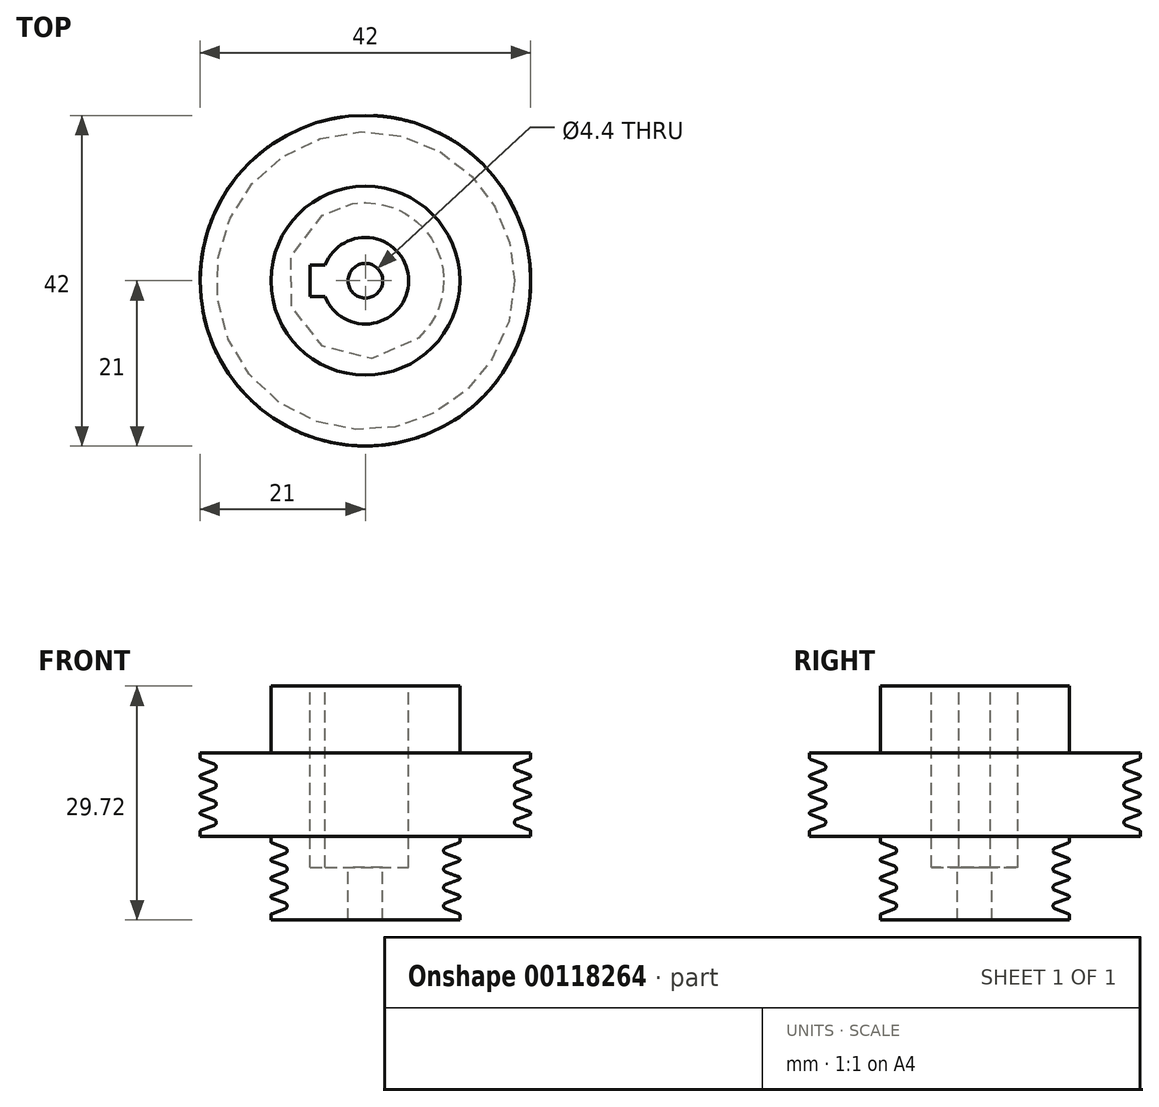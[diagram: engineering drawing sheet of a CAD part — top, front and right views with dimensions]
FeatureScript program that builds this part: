
annotation { "Feature Type Name" : "Feature", "Feature Type Description" : "" }
export const myFeature = defineFeature(function(context is Context, id is Id, definition is map)
    precondition{}
    {
        {
            var Q0;
            Q0=qCreatedBy(makeId("Front.planeOp"),FACE);
            var sketch = newSketch(context, id + "F0", { "sketchPlane" : qUnion([Q0])});
            skLineSegment(sketch, "E0", {"start": v(0, 0) * mm, "end": v(-5.5, 0) * mm, "construction": true});
            skLineSegment(sketch, "E1", {"start": v(-5.5, 0) * mm, "end": v(-21, 0) * mm});
            skLineSegment(sketch, "E2", {"start": v(-21, 1.8) * mm, "end": v(-21, 0.63) * mm, "construction": true});
            skLineSegment(sketch, "E3", {"start": v(-21, 1.8) * mm, "end": v(-19.34, 1.8) * mm, "construction": true});
            skArc(sketch, "E4", {"start": v(-19.2, 1.42) * mm, "mid": v(-18.94, 1.8) * mm, "end": v(-19.2, 2.18) * mm});
            skLineSegment(sketch, "E5", {"start": v(-21, 0.63) * mm, "end": v(-20.8, 0.63) * mm, "construction": true});
            skArc(sketch, "E6", {"start": v(-20.87, 0.82) * mm, "mid": v(-20.96, 0.74) * mm, "end": v(-21, 0.63) * mm});
            skLineSegment(sketch, "E7", {"start": v(-20.87, 0.82) * mm, "end": v(-19.2, 1.42) * mm});
            skLineSegment(sketch, "E8", {"start": v(-19.34, 1.8) * mm, "end": v(-18.94, 1.8) * mm, "construction": true});
            skLineSegment(sketch, "E9.MirrorCS", {"start": v(-20.87, 2.78) * mm, "end": v(-19.2, 2.18) * mm});
            skArc(sketch, "E10.MirrorC", {"start": v(-20.87, 2.78) * mm, "mid": v(-21, 2.97) * mm, "end": v(-20.87, 3.16) * mm});
            skLineSegment(sketch, "E11", {"start": v(-21, 1.8) * mm, "end": v(-21, 10.62) * mm, "construction": true});
            skLineSegment(sketch, "E12", {"start": v(-21, 0.63) * mm, "end": v(-21, 0) * mm});
            skLineSegment(sketch, "E13", {"start": v(-21, 2.97) * mm, "end": v(-20.8, 2.97) * mm, "construction": true});
            skLineSegment(sketch, "E14.MirrorCS", {"start": v(-20.87, 5.12) * mm, "end": v(-19.2, 4.52) * mm});
            skLineSegment(sketch, "E15.MirrorCS", {"start": v(-20.87, 3.16) * mm, "end": v(-19.2, 3.76) * mm});
            skArc(sketch, "E16.MirrorCS", {"start": v(-19.2, 4.52) * mm, "mid": v(-18.94, 4.14) * mm, "end": v(-19.2, 3.76) * mm});
            skArc(sketch, "E17.MirrorC", {"start": v(-20.87, 3.16) * mm, "mid": v(-21, 2.97) * mm, "end": v(-20.87, 2.78) * mm});
            skLineSegment(sketch, "E18", {"start": v(-21.58, 4.14) * mm, "end": v(-21, 4.14) * mm});
            skArc(sketch, "E19.MirrorC", {"start": v(-20.87, 5.12) * mm, "mid": v(-21, 5.3) * mm, "end": v(-20.87, 5.5) * mm});
            skLineSegment(sketch, "E20", {"start": v(-21, 5.3) * mm, "end": v(-20.8, 5.3) * mm, "construction": true});
            skLineSegment(sketch, "E21.MirrorCS", {"start": v(-20.87, 5.5) * mm, "end": v(-19.2, 6.1) * mm});
            skArc(sketch, "E22.MirrorCS", {"start": v(-19.2, 6.1) * mm, "mid": v(-18.94, 6.48) * mm, "end": v(-19.2, 6.86) * mm});
            skLineSegment(sketch, "E23.MirrorCS", {"start": v(-20.87, 7.46) * mm, "end": v(-19.2, 6.86) * mm});
            skArc(sketch, "E24.MirrorCS", {"start": v(-20.87, 7.84) * mm, "mid": v(-21, 7.65) * mm, "end": v(-20.87, 7.46) * mm});
            skLineSegment(sketch, "E25.MirrorCS", {"start": v(-20.87, 7.84) * mm, "end": v(-19.2, 8.44) * mm});
            skArc(sketch, "E26.MirrorCS", {"start": v(-19.2, 9.2) * mm, "mid": v(-18.94, 8.82) * mm, "end": v(-19.2, 8.44) * mm});
            skLineSegment(sketch, "E27.MirrorCS", {"start": v(-20.87, 9.8) * mm, "end": v(-19.2, 9.2) * mm});
            skArc(sketch, "E28.MirrorCS", {"start": v(-20.87, 9.8) * mm, "mid": v(-20.96, 9.87) * mm, "end": v(-21, 9.99) * mm});
            skLineSegment(sketch, "E29.MirrorCS", {"start": v(-21, 9.99) * mm, "end": v(-21, 10.62) * mm});
            skLineSegment(sketch, "E30.MirrorCS", {"start": v(-5.5, 10.62) * mm, "end": v(-21, 10.62) * mm});
            skLineSegment(sketch, "E31.MirrorCS", {"start": v(0, 10.62) * mm, "end": v(-5.5, 10.62) * mm, "construction": true});
            skLineSegment(sketch, "E32", {"start": v(-5.5, 10.62) * mm, "end": v(-5.5, 0) * mm});
            skLineSegment(sketch, "E33", {"start": v(0, 10.62) * mm, "end": v(0, 0) * mm, "construction": true});
            skArc(sketch, "E34", {"start": v(-10.2, -2.18) * mm, "mid": v(-9.94, -1.8) * mm, "end": v(-10.2, -1.42) * mm});
            skArc(sketch, "E35", {"start": v(-12, -0.63) * mm, "mid": v(-11.96, -0.74) * mm, "end": v(-11.87, -0.82) * mm});
            skLineSegment(sketch, "E36", {"start": v(-11.87, -0.82) * mm, "end": v(-10.2, -1.42) * mm});
            skLineSegment(sketch, "E37", {"start": v(-12, -0.63) * mm, "end": v(-12, 0) * mm});
            skLineSegment(sketch, "E38", {"start": v(-12.57, -1.8) * mm, "end": v(-7.09, -1.8) * mm, "construction": true});
            skLineSegment(sketch, "E39.MirrorCS", {"start": v(-11.87, -2.78) * mm, "end": v(-10.2, -2.18) * mm});
            skArc(sketch, "E40.MirrorC", {"start": v(-11.87, -3.16) * mm, "mid": v(-12, -2.97) * mm, "end": v(-11.87, -2.78) * mm});
            skLineSegment(sketch, "E41", {"start": v(-12.6, -2.97) * mm, "end": v(-7.04, -2.97) * mm, "construction": true});
            skArc(sketch, "E42.MirrorC", {"start": v(-11.87, -5.5) * mm, "mid": v(-12, -5.31) * mm, "end": v(-11.87, -5.12) * mm});
            skArc(sketch, "E43.MirrorC", {"start": v(-10.2, -3.76) * mm, "mid": v(-9.94, -4.14) * mm, "end": v(-10.2, -4.52) * mm});
            skLineSegment(sketch, "E44.MirrorCS", {"start": v(-11.87, -3.16) * mm, "end": v(-10.2, -3.76) * mm});
            skLineSegment(sketch, "E45.MirrorCS", {"start": v(-11.87, -5.12) * mm, "end": v(-10.2, -4.52) * mm});
            skLineSegment(sketch, "E46", {"start": v(-12.93, -5.31) * mm, "end": v(-7.12, -5.31) * mm, "construction": true});
            skLineSegment(sketch, "E47.MirrorCS", {"start": v(-11.87, -5.5) * mm, "end": v(-10.2, -6.1) * mm});
            skArc(sketch, "E48.MirrorC", {"start": v(-10.2, -6.86) * mm, "mid": v(-9.94, -6.48) * mm, "end": v(-10.2, -6.1) * mm});
            skLineSegment(sketch, "E49.MirrorCS", {"start": v(-11.87, -7.46) * mm, "end": v(-10.2, -6.86) * mm});
            skArc(sketch, "E50.MirrorC", {"start": v(-11.87, -7.46) * mm, "mid": v(-12, -7.65) * mm, "end": v(-11.87, -7.84) * mm});
            skLineSegment(sketch, "E51.MirrorCS", {"start": v(-11.87, -7.84) * mm, "end": v(-10.2, -8.44) * mm});
            skArc(sketch, "E52.MirrorC", {"start": v(-10.2, -8.44) * mm, "mid": v(-9.94, -8.82) * mm, "end": v(-10.2, -9.2) * mm});
            skLineSegment(sketch, "E53.MirrorCS", {"start": v(-11.87, -9.8) * mm, "end": v(-10.2, -9.2) * mm});
            skArc(sketch, "E54.MirrorC", {"start": v(-12, -10) * mm, "mid": v(-11.96, -9.88) * mm, "end": v(-11.87, -9.8) * mm});
            skLineSegment(sketch, "E55.MirrorCS", {"start": v(-12, -10) * mm, "end": v(-12, -10.62) * mm});
            skLineSegment(sketch, "E56", {"start": v(0, -10.62) * mm, "end": v(0, 0) * mm, "construction": true});
            skLineSegment(sketch, "E57", {"start": v(-5.5, 0) * mm, "end": v(-5.5, -10.62) * mm});
            skLineSegment(sketch, "E58", {"start": v(-12, -10.62) * mm, "end": v(-5.5, -10.62) * mm});
            skLineSegment(sketch, "E59", {"start": v(-5.5, -10.62) * mm, "end": v(0, -10.62) * mm, "construction": true});
            skLineSegment(sketch, "E60", {"start": v(0, 10.62) * mm, "end": v(0, 19.1) * mm});
            skLineSegment(sketch, "E61", {"start": v(0, 19.1) * mm, "end": v(-5.5, 19.1) * mm, "construction": true});
            skLineSegment(sketch, "E62", {"start": v(-5.5, 19.1) * mm, "end": v(-12, 19.1) * mm});
            skLineSegment(sketch, "E63", {"start": v(-12, 19.1) * mm, "end": v(-12, 10.62) * mm});
            skLineSegment(sketch, "E64", {"start": v(-5.5, 19.1) * mm, "end": v(-5.5, 10.62) * mm});
            skLineSegment(sketch, "E65", {"start": v(-5.5, -3.9) * mm, "end": v(-2.2, -3.9) * mm});
            skLineSegment(sketch, "E66", {"start": v(-2.2, -3.9) * mm, "end": v(-2.2, -10.62) * mm});
            skLineSegment(sketch, "E67", {"start": v(-2.2, -10.62) * mm, "end": v(-5.5, -10.62) * mm});
            skLineSegment(sketch, "E68", {"start": v(-20.87, 0.82) * mm, "end": v(-21, 0.77) * mm});
            skLineSegment(sketch, "E69", {"start": v(-21, 0.77) * mm, "end": v(-21, 0.63) * mm});
            skLineSegment(sketch, "E70", {"start": v(-20.87, 2.78) * mm, "end": v(-21, 2.83) * mm});
            skLineSegment(sketch, "E71", {"start": v(-21, 2.83) * mm, "end": v(-21, 2.97) * mm});
            skLineSegment(sketch, "E72", {"start": v(-19.2, 1.42) * mm, "end": v(-18.17, 1.8) * mm, "construction": true});
            skPoint(sketch, "E72.endSnap0", {"position": v(-19.14, 1.8) * mm});
            skLineSegment(sketch, "E73", {"start": v(-19.2, 2.18) * mm, "end": v(-18.17, 1.8) * mm, "construction": true});
            skLineSegment(sketch, "E74", {"start": v(-20.87, 3.16) * mm, "end": v(-21, 3.1) * mm});
            skLineSegment(sketch, "E75", {"start": v(-21, 3.1) * mm, "end": v(-21, 2.97) * mm});
            skSolve(sketch);
        }
        {
            var Q0;
            Q0=makeQuery(id+"F0.imprint","IMPRINT",FACE,{"disambiguationData":[TD([[makeQuery(id+"F0.imprint","IMPRINT",EDGE,{"derivedFrom":sQuery(id+"F0.wireOp",EDGE,"E1")}),-1.0]])]});
            var Q1;
            Q1=makeQuery(id+"F0.imprint","IMPRINT",FACE,{"disambiguationData":[TD([[makeQuery(id+"F0.imprint","IMPRINT",EDGE,{"derivedFrom":sQuery(id+"F0.wireOp",EDGE,"E62")}),1.0]])]});
            var Q2;
            Q2=makeQuery(id+"F0.imprint","IMPRINT",FACE,{"disambiguationData":[TD([[makeQuery(id+"F0.imprint","IMPRINT",EDGE,{"derivedFrom":sQuery(id+"F0.wireOp",EDGE,"E34")}),-1.0]])]});
            var Q3;
            {var subQ2=sQuery(id+"F0.wireOp",EDGE,"E65");Q3=makeQuery(id+"F0.imprint","IMPRINT",FACE,{"disambiguationData":[TD([[makeQuery(id+"F0.imprint","IMPRINT",EDGE,{"derivedFrom":subQ2}),-1.0]])]});}
            var Q4;
            Q4=sQuery(id+"F0.wireOp",EDGE,"E33");
            revolve(context, id + "F1", {"entities" : qUnion([Q0, Q1, Q2, Q3]), "axis" : qUnion([Q4]), "revolveType" : RevolveType.FULL});
        }
        {
            var Q0;
            Q0=makeQuery(id+"F1.opRevolve","SWEPT_FACE",FACE,{"disambiguationData":[OSD([sQuery(id+"F0.wireOp",EDGE,"E62")])]});
            var sketch = newSketch(context, id + "F2", { "sketchPlane" : qUnion([Q0])});
            skCircle(sketch, "E76.0", {"center": v(0, 0) * mm, "radius": 5.5 * mm});
            skLineSegment(sketch, "E77", {"start": v(0, 0) * mm, "end": v(-5.5, 0) * mm, "construction": true});
            skLineSegment(sketch, "E78", {"start": v(-5.5, 0) * mm, "end": v(-7, 0) * mm});
            skLineSegment(sketch, "E79", {"start": v(-7, 0) * mm, "end": v(-7, 2) * mm});
            skLineSegment(sketch, "E80", {"start": v(-7, 2) * mm, "end": v(-5.12, 2) * mm});
            skLineSegment(sketch, "E81.MirrorCS", {"start": v(-7, -2) * mm, "end": v(-5.12, -2) * mm});
            skLineSegment(sketch, "E82.MirrorCS", {"start": v(-7, 0) * mm, "end": v(-7, -2) * mm});
            skLineSegment(sketch, "E83.0", {"start": v(-2.2, 0) * mm, "end": v(-5.5, 0) * mm});
            skLineSegment(sketch, "E83.1", {"start": v(-5.5, 0) * mm, "end": v(-21, 0) * mm});
            skLineSegment(sketch, "E83.2", {"start": v(0, 0) * mm, "end": v(-5.5, 0) * mm});
            skSolve(sketch);
        }
        {
            var Q0;
            {var subQ0=sQuery(id+"F2.wireOp",EDGE,"E81.MirrorCS");Q0=makeQuery(id+"F2.imprint","IMPRINT",FACE,{"disambiguationData":[TD([[makeQuery(id+"F2.imprint","IMPRINT",EDGE,{"derivedFrom":subQ0}),1.0]])]});}
            var Q1;
            {var subQ4=sQuery(id+"F2.wireOp",EDGE,"E79");Q1=makeQuery(id+"F2.imprint","IMPRINT",FACE,{"disambiguationData":[TD([[makeQuery(id+"F2.imprint","IMPRINT",EDGE,{"derivedFrom":subQ4}),-1.0]])]});}
            extrude(context, id + "F3", {"entities" : qUnion([Q0, Q1]), "operationType" : NewBodyOperationType.REMOVE, "oppositeDirection" : true, "depth" : 23 * mm});
        }
    });
